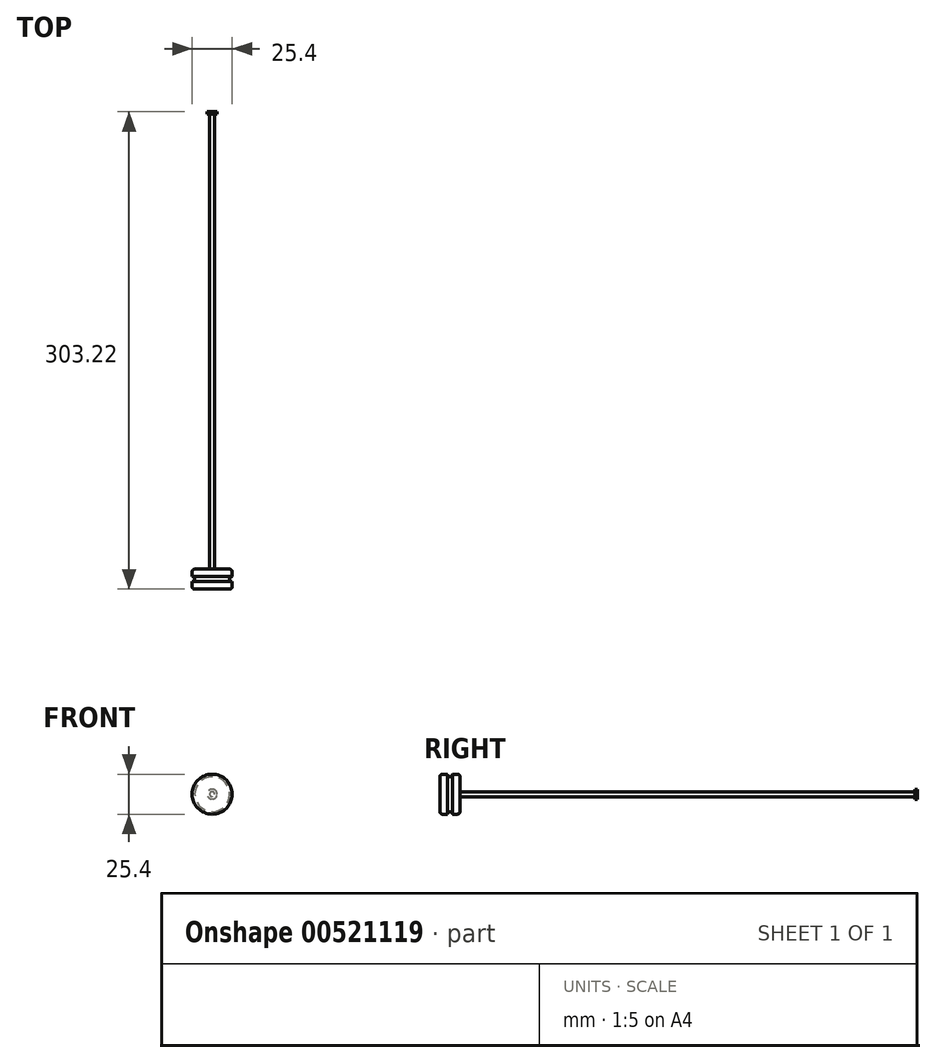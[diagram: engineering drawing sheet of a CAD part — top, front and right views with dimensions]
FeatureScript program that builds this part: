
annotation { "Feature Type Name" : "Feature", "Feature Type Description" : "" }
export const myFeature = defineFeature(function(context is Context, id is Id, definition is map)
    precondition{}
    {
        {
            var Q0;
            Q0=qCreatedBy(makeId("Right.planeOp"),FACE);
            var sketch = newSketch(context, id + "F0", { "sketchPlane" : qUnion([Q0])});
            skLineSegment(sketch, "E0.bottom", {"start": v(-149.23, 12.7) * mm, "end": v(-144.46, 12.7) * mm});
            skLineSegment(sketch, "E0.top", {"start": v(-149.23, 0) * mm, "end": v(-136.53, 0) * mm});
            skLineSegment(sketch, "E0.left", {"start": v(-149.23, 12.7) * mm, "end": v(-149.23, 0) * mm});
            skLineSegment(sketch, "E0.right", {"start": v(-136.53, 12.7) * mm, "end": v(-136.53, 1.59) * mm});
            skLineSegment(sketch, "E1.bottom", {"start": v(-136.53, 1.59) * mm, "end": v(152.4, 1.59) * mm});
            skLineSegment(sketch, "E1.top", {"start": v(-136.53, 0) * mm, "end": v(152.4, 0) * mm});
            skLineSegment(sketch, "E1.right", {"start": v(152.4, 1.59) * mm, "end": v(152.4, 0) * mm});
            skArc(sketch, "E2", {"start": v(-144.46, 12.7) * mm, "mid": v(-142.88, 11.11) * mm, "end": v(-141.29, 12.7) * mm});
            skLineSegment(sketch, "E3.trimOffspring", {"start": v(-141.29, 12.7) * mm, "end": v(-136.53, 12.7) * mm});
            skSolve(sketch);
        }
        {
            var Q0;
            Q0 = qSketchRegion(id + "F0", true);
            var Q1;
            Q1=sQuery(id+"F0.wireOp",EDGE,"E1.top");
            revolve(context, id + "F1", {"entities" : qUnion([Q0]), "axis" : qUnion([Q1]), "revolveType" : RevolveType.FULL});
        }
        {
            var Q0;
            Q0=makeQuery(id+"F1.opRevolve","SWEPT_EDGE",EDGE,{"disambiguationData":[OSD([sQuery(id+"F0.wireOp",EDGE,"E0.right"),sQuery(id+"F0.wireOp",EDGE,"E3.trimOffspring")])]});
            var Q1;
            Q1=makeQuery(id+"F1.opRevolve","SWEPT_EDGE",EDGE,{"disambiguationData":[OSD([sQuery(id+"F0.wireOp",EDGE,"E0.bottom"),sQuery(id+"F0.wireOp",EDGE,"E0.left")])]});
            fillet(context, id + "F2", {"entities" : qUnion([Q0, Q1]), "radius" : 1.59 * mm, "tangentPropagation" : true, "allowEdgeOverflow" : false});
        }
        {
            var Q0;
            Q0=makeQuery(id+"F1.opRevolve","SWEPT_FACE",FACE,{"disambiguationData":[OSD([sQuery(id+"F0.wireOp",EDGE,"E1.right")])]});
            var sketch = newSketch(context, id + "F3", { "sketchPlane" : qUnion([Q0])});
            skCircle(sketch, "E4", {"center": v(0, 0) * mm, "radius": 3.17 * mm});
            skSolve(sketch);
        }
        {
            var Q0;
            Q0 = qSketchRegion(id + "F3", true);
            extrude(context, id + "F4", {"entities" : qUnion([Q0]), "operationType" : NewBodyOperationType.ADD, "depth" : 1.59 * mm, "offsetDistance" : 25.4 * mm});
        }
    });
